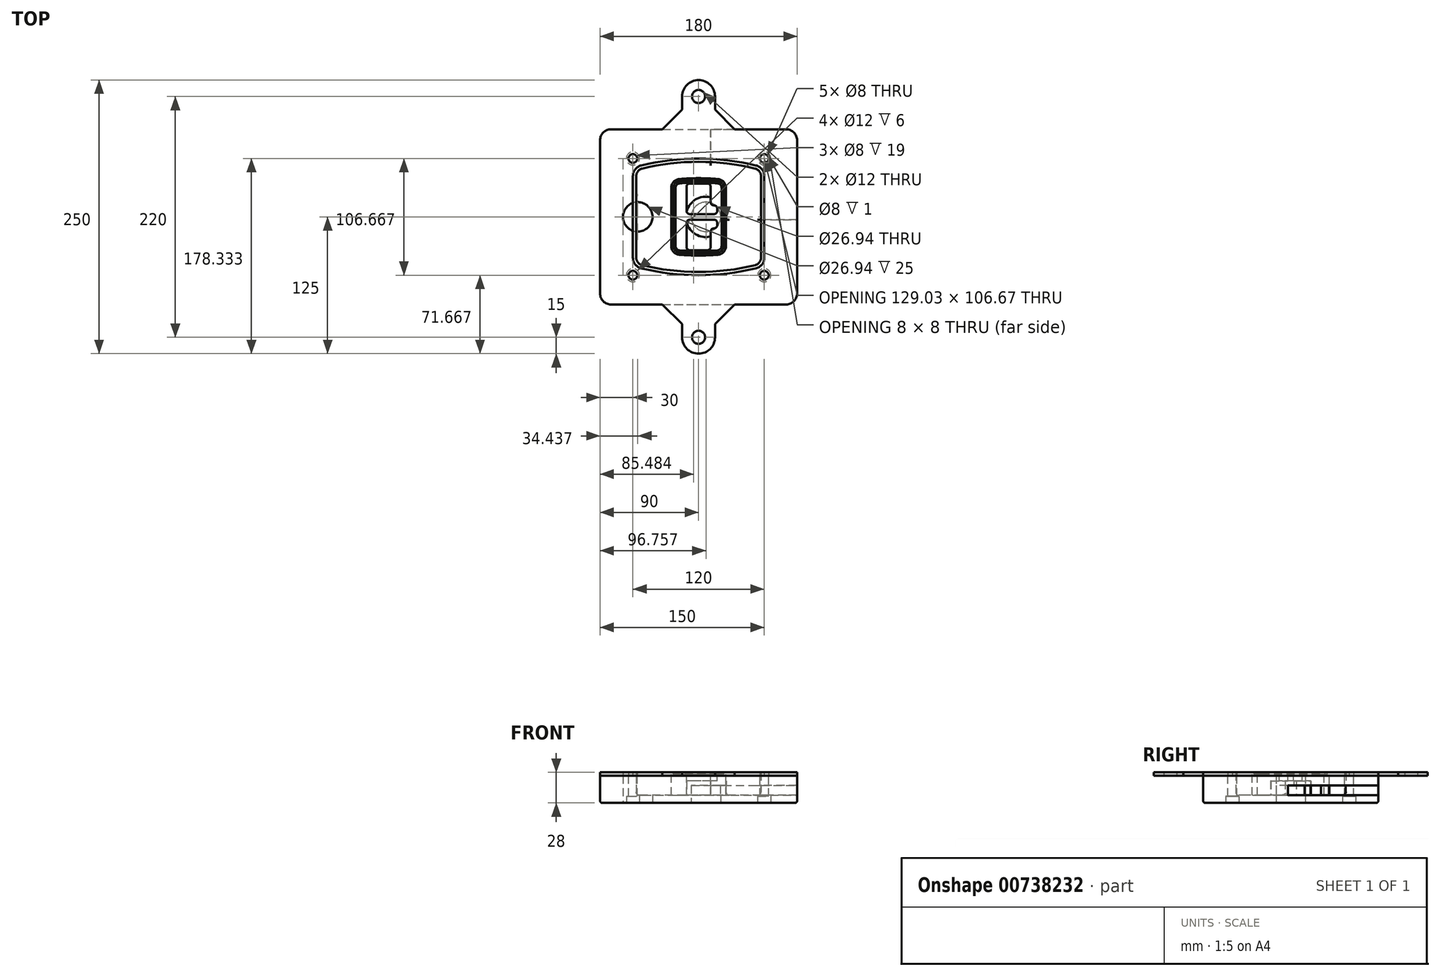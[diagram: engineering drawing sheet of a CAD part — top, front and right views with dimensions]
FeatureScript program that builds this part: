
annotation { "Feature Type Name" : "Feature", "Feature Type Description" : "" }
export const myFeature = defineFeature(function(context is Context, id is Id, definition is map)
    precondition{}
    {
        {
            var Q0;
            Q0=qCreatedBy(makeId("Top.planeOp"),FACE);
            var sketch = newSketch(context, id + "F0", { "sketchPlane" : qUnion([Q0])});
            skPoint(sketch, "E0.rect.middle", {"position": v(0, 0) * mm});
            skLineSegment(sketch, "E1.bottom", {"start": v(-80, -80) * mm, "end": v(80, -80) * mm});
            skLineSegment(sketch, "E1.top", {"start": v(-80, 80) * mm, "end": v(80, 80) * mm});
            skLineSegment(sketch, "E1.left", {"start": v(-90, -70) * mm, "end": v(-90, 70) * mm});
            skLineSegment(sketch, "E1.right", {"start": v(90, -70) * mm, "end": v(90, 70) * mm});
            skLineSegment(sketch, "E2", {"start": v(-90, 80) * mm, "end": v(90, -80) * mm, "construction": true});
            skLineSegment(sketch, "E3", {"start": v(90, 80) * mm, "end": v(-90, -80) * mm, "construction": true});
            skCircle(sketch, "E4", {"center": v(-60, 53.33) * mm, "radius": 4 * mm});
            skCircle(sketch, "E5", {"center": v(60, 53.33) * mm, "radius": 4 * mm});
            skCircle(sketch, "E6", {"center": v(60, -53.33) * mm, "radius": 4 * mm});
            skCircle(sketch, "E7", {"center": v(-60, -53.33) * mm, "radius": 4 * mm});
            skLineSegment(sketch, "E8", {"start": v(-60, 53.33) * mm, "end": v(60, 53.33) * mm, "construction": true});
            skLineSegment(sketch, "E9", {"start": v(60, 53.33) * mm, "end": v(60, -53.33) * mm, "construction": true});
            skLineSegment(sketch, "E10", {"start": v(60, -53.33) * mm, "end": v(-60, -53.33) * mm, "construction": true});
            skLineSegment(sketch, "E11", {"start": v(-60, -53.33) * mm, "end": v(-60, 53.33) * mm, "construction": true});
            skLineSegment(sketch, "E12", {"start": v(-60, 37.3) * mm, "end": v(-60, -37.3) * mm});
            skLineSegment(sketch, "E13", {"start": v(60, 37.3) * mm, "end": v(60, -37.3) * mm});
            skArc(sketch, "E14", {"start": v(52.38, 47.01) * mm, "mid": v(0, 53.33) * mm, "end": v(-52.38, 47.01) * mm});
            skArc(sketch, "E15", {"start": v(-52.38, -47.01) * mm, "mid": v(0, -53.33) * mm, "end": v(52.38, -47.01) * mm});
            skLineSegment(sketch, "E16", {"start": v(-60, 0) * mm, "end": v(60, 0) * mm, "construction": true});
            skPoint(sketch, "E17.visualSharp", {"position": v(-60, -45) * mm});
            skArc(sketch, "E17.filletArc", {"start": v(-60, -37.3) * mm, "mid": v(-57.87, -43.47) * mm, "end": v(-52.38, -47.01) * mm});
            skPoint(sketch, "E18.visualSharp", {"position": v(-60, 45) * mm});
            skArc(sketch, "E18.filletArc", {"start": v(-52.38, 47.01) * mm, "mid": v(-57.87, 43.47) * mm, "end": v(-60, 37.3) * mm});
            skPoint(sketch, "E19.visualSharp", {"position": v(60, 45) * mm});
            skArc(sketch, "E19.filletArc", {"start": v(60, 37.3) * mm, "mid": v(57.87, 43.47) * mm, "end": v(52.38, 47.01) * mm});
            skPoint(sketch, "E20.visualSharp", {"position": v(60, -45) * mm});
            skArc(sketch, "E20.filletArc", {"start": v(52.38, -47.01) * mm, "mid": v(57.87, -43.47) * mm, "end": v(60, -37.3) * mm});
            skPoint(sketch, "E21.visualSharp", {"position": v(-90, 80) * mm});
            skArc(sketch, "E21.filletArc", {"start": v(-80, 80) * mm, "mid": v(-87.07, 77.07) * mm, "end": v(-90, 70) * mm});
            skPoint(sketch, "E22.visualSharp", {"position": v(90, 80) * mm});
            skArc(sketch, "E22.filletArc", {"start": v(90, 70) * mm, "mid": v(87.07, 77.07) * mm, "end": v(80, 80) * mm});
            skPoint(sketch, "E23.visualSharp", {"position": v(90, -80) * mm});
            skArc(sketch, "E23.filletArc", {"start": v(80, -80) * mm, "mid": v(87.07, -77.07) * mm, "end": v(90, -70) * mm});
            skPoint(sketch, "E24.visualSharp", {"position": v(-90, -80) * mm});
            skArc(sketch, "E24.filletArc", {"start": v(-90, -70) * mm, "mid": v(-87.07, -77.07) * mm, "end": v(-80, -80) * mm});
            skArc(sketch, "E25.0", {"start": v(57, 37.3) * mm, "mid": v(55.5, 41.62) * mm, "end": v(51.67, 44.1) * mm});
            skLineSegment(sketch, "E25.1", {"start": v(57, 37.3) * mm, "end": v(57, -37.3) * mm});
            skArc(sketch, "E25.2", {"start": v(51.67, -44.1) * mm, "mid": v(55.5, -41.62) * mm, "end": v(57, -37.3) * mm});
            skArc(sketch, "E25.3", {"start": v(-51.67, -44.1) * mm, "mid": v(0, -50.33) * mm, "end": v(51.67, -44.1) * mm});
            skArc(sketch, "E25.4", {"start": v(-57, -37.3) * mm, "mid": v(-55.5, -41.62) * mm, "end": v(-51.67, -44.1) * mm});
            skArc(sketch, "E25.5", {"start": v(51.67, 44.1) * mm, "mid": v(0, 50.33) * mm, "end": v(-51.67, 44.1) * mm});
            skLineSegment(sketch, "E25.6", {"start": v(-57, 37.3) * mm, "end": v(-57, -37.3) * mm});
            skArc(sketch, "E25.7", {"start": v(-51.67, 44.1) * mm, "mid": v(-55.5, 41.62) * mm, "end": v(-57, 37.3) * mm});
            skArc(sketch, "E26.0", {"start": v(-53.33, 50.9) * mm, "mid": v(-61.01, 45.94) * mm, "end": v(-64, 37.3) * mm});
            skArc(sketch, "E26.1", {"start": v(53.33, 50.9) * mm, "mid": v(0, 57.33) * mm, "end": v(-53.33, 50.9) * mm});
            skArc(sketch, "E26.2", {"start": v(64, 37.3) * mm, "mid": v(61.01, 45.94) * mm, "end": v(53.33, 50.9) * mm});
            skLineSegment(sketch, "E26.3", {"start": v(64, 37.3) * mm, "end": v(64, -37.3) * mm});
            skArc(sketch, "E26.4", {"start": v(53.33, -50.9) * mm, "mid": v(61.01, -45.94) * mm, "end": v(64, -37.3) * mm});
            skLineSegment(sketch, "E26.5", {"start": v(-64, 37.3) * mm, "end": v(-64, -37.3) * mm});
            skArc(sketch, "E26.6", {"start": v(-53.33, -50.9) * mm, "mid": v(0, -57.33) * mm, "end": v(53.33, -50.9) * mm});
            skArc(sketch, "E26.7", {"start": v(-64, -37.3) * mm, "mid": v(-61.01, -45.94) * mm, "end": v(-53.33, -50.9) * mm});
            skSolve(sketch);
        }
        {
            var Q0;
            Q0=makeQuery(id+"F0.imprint","IMPRINT",FACE,{"disambiguationData":[TD([[makeQuery(id+"F0.imprint","IMPRINT",EDGE,{"derivedFrom":sQuery(id+"F0.wireOp",EDGE,"E1.bottom")}),1.0]])]});
            var Q1;
            Q1=makeQuery(id+"F0.imprint","IMPRINT",FACE,{"disambiguationData":[TD([[makeQuery(id+"F0.imprint","IMPRINT",EDGE,{"derivedFrom":sQuery(id+"F0.wireOp",EDGE,"E12")}),1.0]])]});
            var Q2;
            Q2=makeQuery(id+"F0.imprint","IMPRINT",FACE,{"disambiguationData":[TD([[makeQuery(id+"F0.imprint","IMPRINT",EDGE,{"derivedFrom":sQuery(id+"F0.wireOp",EDGE,"E25.0")}),1.0]])]});
            var Q3;
            Q3=makeQuery(id+"F0.imprint","IMPRINT",FACE,{"disambiguationData":[TD([[makeQuery(id+"F0.imprint","IMPRINT",EDGE,{"derivedFrom":sQuery(id+"F0.wireOp",EDGE,"E12")}),-1.0]])]});
            extrude(context, id + "F1", {"entities" : qUnion([Q0, Q1, Q2, Q3]), "oppositeDirection" : true, "depth" : 25 * mm});
        }
        {
            var Q0;
            Q0=makeQuery(id+"F0.imprint","IMPRINT",FACE,{"disambiguationData":[TD([[makeQuery(id+"F0.imprint","IMPRINT",EDGE,{"derivedFrom":sQuery(id+"F0.wireOp",EDGE,"E12")}),1.0]])]});
            extrude(context, id + "F2", {"entities" : qUnion([Q0]), "operationType" : NewBodyOperationType.ADD, "depth" : 3 * mm});
        }
        {
            var Q0;
            Q0=makeQuery(id+"F0.imprint","IMPRINT",FACE,{"disambiguationData":[TD([[makeQuery(id+"F0.imprint","IMPRINT",EDGE,{"derivedFrom":sQuery(id+"F0.wireOp",EDGE,"E25.0")}),1.0]])]});
            extrude(context, id + "F3", {"entities" : qUnion([Q0]), "operationType" : NewBodyOperationType.REMOVE, "oppositeDirection" : true, "depth" : 18 * mm});
        }
        {
            var Q0;
            Q0=makeQuery(id+"F2.opExtrude","CAP_FACE",FACE,{"disambiguationData":[OSD([sQuery(id+"F0.wireOp",EDGE,"E12"),sQuery(id+"F0.wireOp",EDGE,"E13"),sQuery(id+"F0.wireOp",EDGE,"E14"),sQuery(id+"F0.wireOp",EDGE,"E15"),sQuery(id+"F0.wireOp",EDGE,"E17.filletArc"),sQuery(id+"F0.wireOp",EDGE,"E18.filletArc"),sQuery(id+"F0.wireOp",EDGE,"E19.filletArc"),sQuery(id+"F0.wireOp",EDGE,"E20.filletArc"),sQuery(id+"F0.wireOp",EDGE,"E25.0"),sQuery(id+"F0.wireOp",EDGE,"E25.1"),sQuery(id+"F0.wireOp",EDGE,"E25.2"),sQuery(id+"F0.wireOp",EDGE,"E25.3"),sQuery(id+"F0.wireOp",EDGE,"E25.4"),sQuery(id+"F0.wireOp",EDGE,"E25.5"),sQuery(id+"F0.wireOp",EDGE,"E25.6"),sQuery(id+"F0.wireOp",EDGE,"E25.7")])],"isStart":false});
            var sketch = newSketch(context, id + "F4", { "sketchPlane" : qUnion([Q0])});
            skArc(sketch, "E27.0", {"start": v(-17.7, -34.56) * mm, "mid": v(0, -35.33) * mm, "end": v(17.7, -34.56) * mm});
            skArc(sketch, "E28.0", {"start": v(17.7, 34.56) * mm, "mid": v(0, 35.33) * mm, "end": v(-17.7, 34.56) * mm});
            skLineSegment(sketch, "E29", {"start": v(-25, 26.59) * mm, "end": v(-25, -26.59) * mm});
            skLineSegment(sketch, "E30", {"start": v(25, 26.59) * mm, "end": v(25, -26.59) * mm});
            skLineSegment(sketch, "E31", {"start": v(-25, 33.78) * mm, "end": v(25, 33.78) * mm, "construction": true});
            skLineSegment(sketch, "E32", {"start": v(-25, -33.78) * mm, "end": v(25, -33.78) * mm, "construction": true});
            skPoint(sketch, "E33.visualSharp", {"position": v(-25, 33.78) * mm});
            skArc(sketch, "E33.filletArc", {"start": v(-17.7, 34.56) * mm, "mid": v(-22.9, 32) * mm, "end": v(-25, 26.59) * mm});
            skPoint(sketch, "E34.visualSharp", {"position": v(25, 33.78) * mm});
            skArc(sketch, "E34.filletArc", {"start": v(25, 26.59) * mm, "mid": v(22.9, 32) * mm, "end": v(17.7, 34.56) * mm});
            skPoint(sketch, "E35.visualSharp", {"position": v(25, -33.78) * mm});
            skArc(sketch, "E35.filletArc", {"start": v(17.7, -34.56) * mm, "mid": v(22.9, -32) * mm, "end": v(25, -26.59) * mm});
            skPoint(sketch, "E36.visualSharp", {"position": v(-25, -33.78) * mm});
            skArc(sketch, "E36.filletArc", {"start": v(-25, -26.59) * mm, "mid": v(-22.9, -32) * mm, "end": v(-17.7, -34.56) * mm});
            skArc(sketch, "E37.0", {"start": v(51.67, 44.1) * mm, "mid": v(0, 50.33) * mm, "end": v(-51.67, 44.1) * mm});
            skArc(sketch, "E37.1", {"start": v(-51.67, 44.1) * mm, "mid": v(-55.5, 41.62) * mm, "end": v(-57, 37.3) * mm});
            skLineSegment(sketch, "E37.2", {"start": v(-57, 37.3) * mm, "end": v(-57, -37.3) * mm});
            skArc(sketch, "E37.3", {"start": v(-57, -37.3) * mm, "mid": v(-55.5, -41.62) * mm, "end": v(-51.67, -44.1) * mm});
            skArc(sketch, "E37.4", {"start": v(-51.67, -44.1) * mm, "mid": v(0, -50.33) * mm, "end": v(51.67, -44.1) * mm});
            skArc(sketch, "E37.5", {"start": v(51.67, -44.1) * mm, "mid": v(55.5, -41.62) * mm, "end": v(57, -37.3) * mm});
            skLineSegment(sketch, "E37.6", {"start": v(57, 37.3) * mm, "end": v(57, -37.3) * mm});
            skArc(sketch, "E37.7", {"start": v(57, 37.3) * mm, "mid": v(55.5, 41.62) * mm, "end": v(51.67, 44.1) * mm});
            skLineSegment(sketch, "E38.0", {"start": v(23, 26.59) * mm, "end": v(23, -26.59) * mm});
            skArc(sketch, "E38.1", {"start": v(17.53, -32.56) * mm, "mid": v(21.42, -30.64) * mm, "end": v(23, -26.59) * mm});
            skArc(sketch, "E38.2", {"start": v(-17.53, -32.56) * mm, "mid": v(0, -33.33) * mm, "end": v(17.53, -32.56) * mm});
            skArc(sketch, "E38.3", {"start": v(-23, -26.59) * mm, "mid": v(-21.42, -30.64) * mm, "end": v(-17.53, -32.56) * mm});
            skLineSegment(sketch, "E38.4", {"start": v(-23, 26.59) * mm, "end": v(-23, -26.59) * mm});
            skArc(sketch, "E38.5", {"start": v(23, 26.59) * mm, "mid": v(21.42, 30.64) * mm, "end": v(17.53, 32.56) * mm});
            skArc(sketch, "E38.6", {"start": v(-17.53, 32.56) * mm, "mid": v(-21.42, 30.64) * mm, "end": v(-23, 26.59) * mm});
            skArc(sketch, "E38.7", {"start": v(17.53, 32.56) * mm, "mid": v(0, 33.33) * mm, "end": v(-17.53, 32.56) * mm});
            skArc(sketch, "E39.0", {"start": v(21, 26.59) * mm, "mid": v(19.95, 29.29) * mm, "end": v(17.35, 30.57) * mm});
            skLineSegment(sketch, "E39.1", {"start": v(21, 26.59) * mm, "end": v(21, -26.59) * mm});
            skArc(sketch, "E39.2", {"start": v(17.35, -30.57) * mm, "mid": v(19.95, -29.29) * mm, "end": v(21, -26.59) * mm});
            skArc(sketch, "E39.3", {"start": v(-17.35, -30.57) * mm, "mid": v(0, -31.33) * mm, "end": v(17.35, -30.57) * mm});
            skArc(sketch, "E39.4", {"start": v(-21, -26.59) * mm, "mid": v(-19.95, -29.29) * mm, "end": v(-17.35, -30.57) * mm});
            skArc(sketch, "E39.5", {"start": v(17.35, 30.57) * mm, "mid": v(0, 31.33) * mm, "end": v(-17.35, 30.57) * mm});
            skLineSegment(sketch, "E39.6", {"start": v(-21, 26.59) * mm, "end": v(-21, -26.59) * mm});
            skArc(sketch, "E39.7", {"start": v(-17.35, 30.57) * mm, "mid": v(-19.95, 29.29) * mm, "end": v(-21, 26.59) * mm});
            skLineSegment(sketch, "E40", {"start": v(-25, 0) * mm, "end": v(25, 0) * mm, "construction": true});
            skLineSegment(sketch, "E41", {"start": v(-11, 5.5) * mm, "end": v(-11, 27.5) * mm});
            skLineSegment(sketch, "E42", {"start": v(-8, 30.5) * mm, "end": v(8, 30.5) * mm});
            skLineSegment(sketch, "E43", {"start": v(11, 27.5) * mm, "end": v(11, 13.5) * mm});
            skLineSegment(sketch, "E44", {"start": v(14, 10.5) * mm, "end": v(14, 10.5) * mm});
            skLineSegment(sketch, "E45", {"start": v(17, 7.5) * mm, "end": v(17, 5.5) * mm});
            skLineSegment(sketch, "E46", {"start": v(14, 2.5) * mm, "end": v(-8, 2.5) * mm});
            skPoint(sketch, "E47.visualSharp", {"position": v(-11, 30.5) * mm});
            skArc(sketch, "E47.filletArc", {"start": v(-8, 30.5) * mm, "mid": v(-10.12, 29.62) * mm, "end": v(-11, 27.5) * mm});
            skPoint(sketch, "E48.visualSharp", {"position": v(11, 30.5) * mm});
            skArc(sketch, "E48.filletArc", {"start": v(11, 27.5) * mm, "mid": v(10.12, 29.62) * mm, "end": v(8, 30.5) * mm});
            skPoint(sketch, "E49.visualSharp", {"position": v(11, 10.5) * mm});
            skArc(sketch, "E49.filletArc", {"start": v(11, 13.5) * mm, "mid": v(11.88, 11.38) * mm, "end": v(14, 10.5) * mm});
            skPoint(sketch, "E50.visualSharp", {"position": v(17, 10.5) * mm});
            skArc(sketch, "E50.filletArc", {"start": v(17, 7.5) * mm, "mid": v(16.12, 9.62) * mm, "end": v(14, 10.5) * mm});
            skPoint(sketch, "E51.visualSharp", {"position": v(17, 2.5) * mm});
            skArc(sketch, "E51.filletArc", {"start": v(14, 2.5) * mm, "mid": v(16.12, 3.38) * mm, "end": v(17, 5.5) * mm});
            skPoint(sketch, "E52.visualSharp", {"position": v(-11, 2.5) * mm});
            skArc(sketch, "E52.filletArc", {"start": v(-11, 5.5) * mm, "mid": v(-10.12, 3.38) * mm, "end": v(-8, 2.5) * mm});
            skLineSegment(sketch, "E53.0.MirrorCS", {"start": v(14, -2.5) * mm, "end": v(-8, -2.5) * mm});
            skArc(sketch, "E54.0.MirrorCS", {"start": v(-11, -5.5) * mm, "mid": v(-10.12, -3.38) * mm, "end": v(-8, -2.5) * mm});
            skLineSegment(sketch, "E55.0.MirrorCS", {"start": v(-11, -5.5) * mm, "end": v(-11, -27.5) * mm});
            skArc(sketch, "E56.0.MirrorCS", {"start": v(-8, -30.5) * mm, "mid": v(-10.12, -29.62) * mm, "end": v(-11, -27.5) * mm});
            skLineSegment(sketch, "E57.0.MirrorCS", {"start": v(-8, -30.5) * mm, "end": v(8, -30.5) * mm});
            skArc(sketch, "E58.0.MirrorCS", {"start": v(11, -27.5) * mm, "mid": v(10.12, -29.62) * mm, "end": v(8, -30.5) * mm});
            skLineSegment(sketch, "E59.0.MirrorCS", {"start": v(11, -27.5) * mm, "end": v(11, -13.5) * mm});
            skArc(sketch, "E60.0.MirrorCS", {"start": v(11, -13.5) * mm, "mid": v(11.88, -11.38) * mm, "end": v(14, -10.5) * mm});
            skArc(sketch, "E61.0.MirrorCS", {"start": v(17, -7.5) * mm, "mid": v(16.12, -9.62) * mm, "end": v(14, -10.5) * mm});
            skLineSegment(sketch, "E62.0.MirrorCS", {"start": v(17, -7.5) * mm, "end": v(17, -5.5) * mm});
            skArc(sketch, "E63.0.MirrorCS", {"start": v(14, -2.5) * mm, "mid": v(16.12, -3.38) * mm, "end": v(17, -5.5) * mm});
            skSolve(sketch);
        }
        {
            var Q0;
            Q0=makeQuery(id+"F4.imprint","IMPRINT",FACE,{"disambiguationData":[TD([[makeQuery(id+"F4.imprint","IMPRINT",EDGE,{"derivedFrom":sQuery(id+"F4.wireOp",EDGE,"E27.0")}),1.0]])]});
            var Q1;
            Q1=makeQuery(id+"F4.imprint","IMPRINT",FACE,{"disambiguationData":[TD([[makeQuery(id+"F4.imprint","IMPRINT",EDGE,{"derivedFrom":sQuery(id+"F4.wireOp",EDGE,"E38.0")}),-1.0]])]});
            var Q2;
            Q2=makeQuery(id+"F4.imprint","IMPRINT",FACE,{"disambiguationData":[TD([[makeQuery(id+"F4.imprint","IMPRINT",EDGE,{"derivedFrom":sQuery(id+"F4.wireOp",EDGE,"E39.0")}),1.0]])]});
            extrude(context, id + "F5", {"entities" : qUnion([Q0, Q1, Q2]), "operationType" : NewBodyOperationType.ADD, "endBound" : BoundingType.UP_TO_NEXT, "oppositeDirection" : true, "depth" : 25 * mm});
        }
        {
            var Q0;
            Q0=makeQuery(id+"F4.imprint","IMPRINT",FACE,{"disambiguationData":[TD([[makeQuery(id+"F4.imprint","IMPRINT",EDGE,{"derivedFrom":sQuery(id+"F4.wireOp",EDGE,"E38.0")}),-1.0]])]});
            extrude(context, id + "F6", {"entities" : qUnion([Q0]), "operationType" : NewBodyOperationType.REMOVE, "oppositeDirection" : true, "depth" : 2 * mm});
        }
        {
            var Q0;
            Q0=makeQuery(id+"F1.opExtrude","CAP_FACE",FACE,{"disambiguationData":[OSD([sQuery(id+"F0.wireOp",EDGE,"E1.bottom"),sQuery(id+"F0.wireOp",EDGE,"E1.top"),sQuery(id+"F0.wireOp",EDGE,"E1.left"),sQuery(id+"F0.wireOp",EDGE,"E1.right"),sQuery(id+"F0.wireOp",EDGE,"E4"),sQuery(id+"F0.wireOp",EDGE,"E5"),sQuery(id+"F0.wireOp",EDGE,"E6"),sQuery(id+"F0.wireOp",EDGE,"E7"),sQuery(id+"F0.wireOp",EDGE,"E21.filletArc"),sQuery(id+"F0.wireOp",EDGE,"E22.filletArc"),sQuery(id+"F0.wireOp",EDGE,"E23.filletArc"),sQuery(id+"F0.wireOp",EDGE,"E24.filletArc")])],"isStart":false});
            var sketch = newSketch(context, id + "F7", { "sketchPlane" : qUnion([Q0])});
            skCircle(sketch, "E64", {"center": v(6.76, 0) * mm, "radius": 13.47 * mm});
            skCircle(sketch, "E65", {"center": v(-55.56, 0) * mm, "radius": 13.47 * mm});
            skLineSegment(sketch, "E66", {"start": v(90, 0) * mm, "end": v(-90, 0) * mm});
            skCircle(sketch, "E67", {"center": v(6.76, 0) * mm, "radius": 18.47 * mm});
            skCircle(sketch, "E68", {"center": v(60, -53.33) * mm, "radius": 6 * mm});
            skCircle(sketch, "E69", {"center": v(-60, -53.33) * mm, "radius": 6 * mm});
            skCircle(sketch, "E70", {"center": v(-60, 53.33) * mm, "radius": 6 * mm});
            skCircle(sketch, "E71", {"center": v(60, 53.33) * mm, "radius": 6 * mm});
            skSolve(sketch);
        }
        {
            var Q0;
            {var subQ1=sQuery(id+"F7.wireOp",EDGE,"E66");var subQ4=sQuery(id+"F7.wireOp",EDGE,"E64");var subQ6=makeQuery(id+"F7.imprint","INTERSECT",VERTEX,{"disambiguationData":[OD(0.0)],"derivedFrom":[subQ4,subQ1]});Q0=makeQuery(id+"F7.imprint","IMPRINT",FACE,{"disambiguationData":[TD([[makeQuery(id+"F7.imprint","IMPRINT",EDGE,{"disambiguationData":[TD([[subQ6,-1.0]])],"derivedFrom":subQ4}),-1.0]])]});}
            var Q1;
            {var subQ0=sQuery(id+"F7.wireOp",EDGE,"E66");var subQ1=sQuery(id+"F7.wireOp",EDGE,"E64");var subQ3=makeQuery(id+"F7.imprint","INTERSECT",VERTEX,{"disambiguationData":[OD(0.0)],"derivedFrom":[subQ1,subQ0]});Q1=makeQuery(id+"F7.imprint","IMPRINT",FACE,{"disambiguationData":[TD([[makeQuery(id+"F7.imprint","IMPRINT",EDGE,{"disambiguationData":[TD([[subQ3,-1.0]])],"derivedFrom":subQ1}),1.0]])]});}
            var Q2;
            {var subQ0=sQuery(id+"F7.wireOp",EDGE,"E66");var subQ1=sQuery(id+"F7.wireOp",EDGE,"E64");var subQ3=makeQuery(id+"F7.imprint","INTERSECT",VERTEX,{"disambiguationData":[OD(0.0)],"derivedFrom":[subQ1,subQ0]});Q2=makeQuery(id+"F7.imprint","IMPRINT",FACE,{"disambiguationData":[TD([[makeQuery(id+"F7.imprint","IMPRINT",EDGE,{"disambiguationData":[TD([[subQ3,1.0]])],"derivedFrom":subQ1}),1.0]])]});}
            var Q3;
            {var subQ1=sQuery(id+"F7.wireOp",EDGE,"E66");var subQ4=sQuery(id+"F7.wireOp",EDGE,"E64");var subQ6=makeQuery(id+"F7.imprint","INTERSECT",VERTEX,{"disambiguationData":[OD(0.0)],"derivedFrom":[subQ4,subQ1]});Q3=makeQuery(id+"F7.imprint","IMPRINT",FACE,{"disambiguationData":[TD([[makeQuery(id+"F7.imprint","IMPRINT",EDGE,{"disambiguationData":[TD([[subQ6,1.0]])],"derivedFrom":subQ4}),-1.0]])]});}
            extrude(context, id + "F8", {"entities" : qUnion([Q0, Q1, Q2, Q3]), "operationType" : NewBodyOperationType.ADD, "oppositeDirection" : true, "depth" : 20 * mm});
        }
        {
            var Q0;
            {var subQ0=sQuery(id+"F7.wireOp",EDGE,"E66");var subQ1=sQuery(id+"F7.wireOp",EDGE,"E64");var subQ3=makeQuery(id+"F7.imprint","INTERSECT",VERTEX,{"disambiguationData":[OD(0.0)],"derivedFrom":[subQ1,subQ0]});Q0=makeQuery(id+"F7.imprint","IMPRINT",FACE,{"disambiguationData":[TD([[makeQuery(id+"F7.imprint","IMPRINT",EDGE,{"disambiguationData":[TD([[subQ3,-1.0]])],"derivedFrom":subQ1}),1.0]])]});}
            var Q1;
            {var subQ0=sQuery(id+"F7.wireOp",EDGE,"E66");var subQ1=sQuery(id+"F7.wireOp",EDGE,"E64");var subQ3=makeQuery(id+"F7.imprint","INTERSECT",VERTEX,{"disambiguationData":[OD(0.0)],"derivedFrom":[subQ1,subQ0]});Q1=makeQuery(id+"F7.imprint","IMPRINT",FACE,{"disambiguationData":[TD([[makeQuery(id+"F7.imprint","IMPRINT",EDGE,{"disambiguationData":[TD([[subQ3,1.0]])],"derivedFrom":subQ1}),1.0]])]});}
            extrude(context, id + "F9", {"entities" : qUnion([Q0, Q1]), "operationType" : NewBodyOperationType.REMOVE, "oppositeDirection" : true, "depth" : 16 * mm});
        }
        {
            var Q0;
            {var subQ0=sQuery(id+"F7.wireOp",EDGE,"E66");var subQ1=sQuery(id+"F7.wireOp",EDGE,"E65");var subQ3=makeQuery(id+"F7.imprint","INTERSECT",VERTEX,{"disambiguationData":[OD(0.0)],"derivedFrom":[subQ1,subQ0]});Q0=makeQuery(id+"F7.imprint","IMPRINT",FACE,{"disambiguationData":[TD([[makeQuery(id+"F7.imprint","IMPRINT",EDGE,{"disambiguationData":[TD([[subQ3,-1.0]])],"derivedFrom":subQ1}),1.0]])]});}
            var Q1;
            {var subQ0=sQuery(id+"F7.wireOp",EDGE,"E66");var subQ1=sQuery(id+"F7.wireOp",EDGE,"E65");var subQ3=makeQuery(id+"F7.imprint","INTERSECT",VERTEX,{"disambiguationData":[OD(0.0)],"derivedFrom":[subQ1,subQ0]});Q1=makeQuery(id+"F7.imprint","IMPRINT",FACE,{"disambiguationData":[TD([[makeQuery(id+"F7.imprint","IMPRINT",EDGE,{"disambiguationData":[TD([[subQ3,1.0]])],"derivedFrom":subQ1}),1.0]])]});}
            extrude(context, id + "F10", {"entities" : qUnion([Q0, Q1]), "operationType" : NewBodyOperationType.REMOVE, "oppositeDirection" : true, "depth" : 25 * mm});
        }
        {
            var Q0;
            Q0=makeQuery(id+"F7.imprint","IMPRINT",FACE,{"disambiguationData":[TD([[makeQuery(id+"F7.imprint","IMPRINT",EDGE,{"derivedFrom":sQuery(id+"F7.wireOp",EDGE,"E68")}),1.0]])]});
            var Q1;
            Q1=makeQuery(id+"F7.imprint","IMPRINT",FACE,{"disambiguationData":[TD([[makeQuery(id+"F7.imprint","IMPRINT",EDGE,{"derivedFrom":makeQuery(id+"F1.opExtrude","CAP_EDGE",EDGE,{"disambiguationData":[OSD([sQuery(id+"F0.wireOp",EDGE,"E5")])],"isStart":false})}),-1.0]])]});
            var Q2;
            Q2=makeQuery(id+"F7.imprint","IMPRINT",FACE,{"disambiguationData":[TD([[makeQuery(id+"F7.imprint","IMPRINT",EDGE,{"derivedFrom":sQuery(id+"F7.wireOp",EDGE,"E69")}),1.0]])]});
            var Q3;
            Q3=makeQuery(id+"F7.imprint","IMPRINT",FACE,{"disambiguationData":[TD([[makeQuery(id+"F7.imprint","IMPRINT",EDGE,{"derivedFrom":makeQuery(id+"F1.opExtrude","CAP_EDGE",EDGE,{"disambiguationData":[OSD([sQuery(id+"F0.wireOp",EDGE,"E4")])],"isStart":false})}),-1.0]])]});
            var Q4;
            Q4=makeQuery(id+"F7.imprint","IMPRINT",FACE,{"disambiguationData":[TD([[makeQuery(id+"F7.imprint","IMPRINT",EDGE,{"derivedFrom":sQuery(id+"F7.wireOp",EDGE,"E70")}),1.0]])]});
            var Q5;
            Q5=makeQuery(id+"F7.imprint","IMPRINT",FACE,{"disambiguationData":[TD([[makeQuery(id+"F7.imprint","IMPRINT",EDGE,{"derivedFrom":makeQuery(id+"F1.opExtrude","CAP_EDGE",EDGE,{"disambiguationData":[OSD([sQuery(id+"F0.wireOp",EDGE,"E7")])],"isStart":false})}),-1.0]])]});
            var Q6;
            Q6=makeQuery(id+"F7.imprint","IMPRINT",FACE,{"disambiguationData":[TD([[makeQuery(id+"F7.imprint","IMPRINT",EDGE,{"derivedFrom":sQuery(id+"F7.wireOp",EDGE,"E71")}),1.0]])]});
            var Q7;
            Q7=makeQuery(id+"F7.imprint","IMPRINT",FACE,{"disambiguationData":[TD([[makeQuery(id+"F7.imprint","IMPRINT",EDGE,{"derivedFrom":makeQuery(id+"F1.opExtrude","CAP_EDGE",EDGE,{"disambiguationData":[OSD([sQuery(id+"F0.wireOp",EDGE,"E6")])],"isStart":false})}),-1.0]])]});
            extrude(context, id + "F11", {"entities" : qUnion([Q0, Q1, Q2, Q3, Q4, Q5, Q6, Q7]), "operationType" : NewBodyOperationType.REMOVE, "oppositeDirection" : true, "depth" : 6 * mm});
        }
        {
            var Q0;
            Q0=makeQuery(id+"F9.boolean.opBoolean","COPY",FACE,{"derivedFrom":makeQuery(id+"F9.opExtrude","CAP_FACE",FACE,{"disambiguationData":[OSD([sQuery(id+"F7.wireOp",EDGE,"E64")])],"isStart":false})});
            var sketch = newSketch(context, id + "F12", { "sketchPlane" : qUnion([Q0])});
            skArc(sketch, "E72.0", {"start": v(11, -88.19) * mm, "mid": v(97.1, -83.6) * mm, "end": v(92.5, 2.5) * mm});
            skLineSegment(sketch, "E72.1", {"start": v(11, -17.97) * mm, "end": v(11, -17.97) * mm});
            skLineSegment(sketch, "E73", {"start": v(92.5, -105.13) * mm, "end": v(102.3, -105.13) * mm});
            skLineSegment(sketch, "E74.0", {"start": v(92.5, 2.5) * mm, "end": v(14, 2.5) * mm});
            skArc(sketch, "E74.1", {"start": v(14, 2.5) * mm, "mid": v(16.12, 3.38) * mm, "end": v(17, 5.5) * mm});
            skLineSegment(sketch, "E74.2", {"start": v(17, 7.5) * mm, "end": v(17, 5.5) * mm});
            skArc(sketch, "E74.3", {"start": v(17, 7.5) * mm, "mid": v(16.12, 9.62) * mm, "end": v(14, 10.5) * mm});
            skArc(sketch, "E74.4", {"start": v(11, 13.5) * mm, "mid": v(11.88, 11.38) * mm, "end": v(14, 10.5) * mm});
            skLineSegment(sketch, "E74.5", {"start": v(11, 13.5) * mm, "end": v(11, -88.19) * mm});
            skLineSegment(sketch, "E74.7", {"start": v(92.5, -2.5) * mm, "end": v(14, -2.5) * mm});
            skArc(sketch, "E74.8", {"start": v(14, -2.5) * mm, "mid": v(16.12, -3.38) * mm, "end": v(17, -5.5) * mm});
            skLineSegment(sketch, "E74.9", {"start": v(17, -7.5) * mm, "end": v(17, -5.5) * mm});
            skArc(sketch, "E74.10", {"start": v(17, -7.5) * mm, "mid": v(16.12, -9.62) * mm, "end": v(14, -10.5) * mm});
            skArc(sketch, "E74.11", {"start": v(11, -13.5) * mm, "mid": v(11.88, -11.38) * mm, "end": v(14, -10.5) * mm});
            skLineSegment(sketch, "E74.12", {"start": v(11, -17.97) * mm, "end": v(11, -13.5) * mm});
            skPoint(sketch, "E75.orphan", {"position": v(11, -27.5) * mm});
            skPoint(sketch, "E76.orphan", {"position": v(-8, -2.5) * mm});
            skPoint(sketch, "E77.orphan", {"position": v(-8, 2.5) * mm});
            skPoint(sketch, "E78.orphan", {"position": v(11, 27.5) * mm});
            skSolve(sketch);
        }
        {
            var Q0;
            {var subQ7=sQuery(id+"F12.wireOp",EDGE,"E72.0");var subQ14=sQuery(id+"F12.wireOp",EDGE,"E72.1");var subQ16=sQuery(id+"F12.wireOp",EDGE,"E74.1");var subQ18=sQuery(id+"F12.wireOp",EDGE,"E74.8");Q0=qUnion([makeQuery(id+"F12.imprint","IMPRINT",FACE,{"disambiguationData":[TD([[makeQuery(id+"F12.imprint","IMPRINT",EDGE,{"derivedFrom":subQ7}),1.0]])]}),makeQuery(id+"F12.imprint","IMPRINT",FACE,{"disambiguationData":[TD([[makeQuery(id+"F12.imprint","IMPRINT",EDGE,{"derivedFrom":subQ14}),1.0]])]}),makeQuery(id+"F12.imprint","IMPRINT",FACE,{"disambiguationData":[TD([[makeQuery(id+"F12.imprint","IMPRINT",EDGE,{"derivedFrom":subQ16}),1.0]])]}),makeQuery(id+"F12.imprint","IMPRINT",FACE,{"disambiguationData":[TD([[makeQuery(id+"F12.imprint","IMPRINT",EDGE,{"derivedFrom":subQ18}),-1.0]])]})]);}
            var Q1;
            Q1=makeQuery(id+"F5.boolean.opBoolean","SPLIT",FACE,{"disambiguationData":[TD([makeQuery(id+"F5.opExtrude","SWEPT_FACE",FACE,{"disambiguationData":[OSD([sQuery(id+"F4.wireOp",EDGE,"E41")])]})])],"derivedFrom":makeQuery(id+"F3.boolean.opBoolean","COPY",FACE,{"derivedFrom":makeQuery(id+"F3.opExtrude","CAP_FACE",FACE,{"disambiguationData":[OSD([sQuery(id+"F0.wireOp",EDGE,"E25.0"),sQuery(id+"F0.wireOp",EDGE,"E25.1"),sQuery(id+"F0.wireOp",EDGE,"E25.2"),sQuery(id+"F0.wireOp",EDGE,"E25.3"),sQuery(id+"F0.wireOp",EDGE,"E25.4"),sQuery(id+"F0.wireOp",EDGE,"E25.5"),sQuery(id+"F0.wireOp",EDGE,"E25.6"),sQuery(id+"F0.wireOp",EDGE,"E25.7")])],"isStart":false})})});
            extrude(context, id + "F13", {"entities" : qUnion([Q0]), "operationType" : NewBodyOperationType.REMOVE, "endBound" : BoundingType.UP_TO_SURFACE, "endBoundEntityFace" : qUnion([Q1]), "depth" : 25 * mm});
        }
        {
            var Q0;
            Q0=makeQuery(id+"F3.boolean.opBoolean","COPY",EDGE,{"derivedFrom":makeQuery(id+"F3.opExtrude","CAP_EDGE",EDGE,{"disambiguationData":[OSD([sQuery(id+"F0.wireOp",EDGE,"E25.6")])],"isStart":false})});
            var Q1;
            Q1=makeQuery(id+"F8.boolean.opBoolean","INTERSECT",EDGE,{"derivedFrom":[makeQuery(id+"F5.opExtrude","SWEPT_FACE",FACE,{"disambiguationData":[OSD([sQuery(id+"F4.wireOp",EDGE,"E30")])]}),makeQuery(id+"F8.opExtrude","CAP_FACE",FACE,{"disambiguationData":[OSD([sQuery(id+"F7.wireOp",EDGE,"E67")])],"isStart":false})]});
            var Q2;
            Q2=makeQuery(id+"F8.boolean.opBoolean","INTERSECT",EDGE,{"disambiguationData":[OD(1.0)],"derivedFrom":[makeQuery(id+"F5.opExtrude","SWEPT_FACE",FACE,{"disambiguationData":[OSD([sQuery(id+"F4.wireOp",EDGE,"E30")])]}),makeQuery(id+"F8.opExtrude","SWEPT_FACE",FACE,{"disambiguationData":[OSD([sQuery(id+"F7.wireOp",EDGE,"E67")])]})]});
            var Q3;
            {var subQ0=makeQuery(id+"F3.boolean.opBoolean","COPY",FACE,{"derivedFrom":makeQuery(id+"F3.opExtrude","CAP_FACE",FACE,{"disambiguationData":[OSD([sQuery(id+"F0.wireOp",EDGE,"E25.0"),sQuery(id+"F0.wireOp",EDGE,"E25.1"),sQuery(id+"F0.wireOp",EDGE,"E25.2"),sQuery(id+"F0.wireOp",EDGE,"E25.3"),sQuery(id+"F0.wireOp",EDGE,"E25.4"),sQuery(id+"F0.wireOp",EDGE,"E25.5"),sQuery(id+"F0.wireOp",EDGE,"E25.6"),sQuery(id+"F0.wireOp",EDGE,"E25.7")])],"isStart":false})});var subQ1=sQuery(id+"F4.wireOp",EDGE,"E30");Q3=makeQuery(id+"F8.boolean.opBoolean","SPLIT",EDGE,{"disambiguationData":[TD([makeQuery(id+"F5.opExtrude","SWEPT_FACE",FACE,{"disambiguationData":[OSD([sQuery(id+"F4.wireOp",EDGE,"E35.filletArc")])]})])],"derivedFrom":makeQuery(id+"F5.opExtrude","TWEAK_EDGE",EDGE,{"derivedFrom":[subQ0,makeQuery(id+"F4.imprint","IMPRINT",EDGE,{"derivedFrom":subQ1})]})});}
            var Q4;
            {var subQ0=sQuery(id+"F0.wireOp",EDGE,"E25.0");var subQ1=sQuery(id+"F0.wireOp",EDGE,"E25.1");var subQ2=sQuery(id+"F0.wireOp",EDGE,"E25.2");var subQ3=sQuery(id+"F0.wireOp",EDGE,"E25.3");var subQ4=sQuery(id+"F0.wireOp",EDGE,"E25.4");var subQ5=sQuery(id+"F0.wireOp",EDGE,"E25.5");var subQ6=sQuery(id+"F0.wireOp",EDGE,"E25.6");var subQ7=sQuery(id+"F0.wireOp",EDGE,"E25.7");Q4=makeQuery(id+"F8.boolean.opBoolean","INTERSECT",EDGE,{"derivedFrom":[makeQuery(id+"F5.boolean.opBoolean","SPLIT",FACE,{"disambiguationData":[TD([makeQuery(id+"F2.opExtrude","SWEPT_FACE",FACE,{"disambiguationData":[OSD([subQ0])]})])],"derivedFrom":makeQuery(id+"F3.boolean.opBoolean","COPY",FACE,{"derivedFrom":makeQuery(id+"F3.opExtrude","CAP_FACE",FACE,{"disambiguationData":[OSD([subQ0,subQ1,subQ2,subQ3,subQ4,subQ5,subQ6,subQ7])],"isStart":false})})}),makeQuery(id+"F8.opExtrude","SWEPT_FACE",FACE,{"disambiguationData":[OSD([sQuery(id+"F7.wireOp",EDGE,"E67")])]})]});}
            var Q5;
            Q5=makeQuery(id+"F8.boolean.opBoolean","INTERSECT",EDGE,{"disambiguationData":[OD(0.0)],"derivedFrom":[makeQuery(id+"F5.opExtrude","SWEPT_FACE",FACE,{"disambiguationData":[OSD([sQuery(id+"F4.wireOp",EDGE,"E30")])]}),makeQuery(id+"F8.opExtrude","SWEPT_FACE",FACE,{"disambiguationData":[OSD([sQuery(id+"F7.wireOp",EDGE,"E67")])]})]});
            fillet(context, id + "F14", {"entities" : qUnion([Q0, Q1, Q2, Q3, Q4, Q5]), "radius" : 3 * mm, "tangentPropagation" : true, "allowEdgeOverflow" : false});
        }
        {
            var Q0;
            Q0=makeQuery(id+"F1.opExtrude","CAP_EDGE",EDGE,{"disambiguationData":[OSD([sQuery(id+"F0.wireOp",EDGE,"E1.bottom")])],"isStart":false});
            fillet(context, id + "F15", {"entities" : qUnion([Q0]), "radius" : 2 * mm, "tangentPropagation" : true, "allowEdgeOverflow" : false});
        }
        {
            var Q0;
            {var subQ0=sQuery(id+"F0.wireOp",EDGE,"E21.filletArc");var subQ1=sQuery(id+"F0.wireOp",EDGE,"E7");var subQ2=sQuery(id+"F0.wireOp",EDGE,"E6");var subQ3=sQuery(id+"F0.wireOp",EDGE,"E5");var subQ4=sQuery(id+"F0.wireOp",EDGE,"E4");var subQ5=sQuery(id+"F0.wireOp",EDGE,"E22.filletArc");var subQ6=sQuery(id+"F0.wireOp",EDGE,"E1.bottom");var subQ7=sQuery(id+"F0.wireOp",EDGE,"E1.right");var subQ8=sQuery(id+"F0.wireOp",EDGE,"E1.top");var subQ9=sQuery(id+"F0.wireOp",EDGE,"E1.left");var subQ10=sQuery(id+"F0.wireOp",EDGE,"E23.filletArc");var subQ11=sQuery(id+"F0.wireOp",EDGE,"E24.filletArc");Q0=makeQuery(id+"F2.boolean.opBoolean","SPLIT",FACE,{"disambiguationData":[TD([makeQuery(id+"F1.opExtrude","SWEPT_FACE",FACE,{"disambiguationData":[OSD([subQ6])]})])],"derivedFrom":makeQuery(id+"F1.opExtrude","CAP_FACE",FACE,{"disambiguationData":[OSD([subQ6,subQ8,subQ9,subQ7,subQ4,subQ3,subQ2,subQ1,subQ0,subQ5,subQ10,subQ11])],"isStart":true})});}
            var sketch = newSketch(context, id + "F16", { "sketchPlane" : qUnion([Q0])});
            skLineSegment(sketch, "E79.0", {"start": v(-80, 80) * mm, "end": v(80, 80) * mm});
            skLineSegment(sketch, "E79.1", {"start": v(-90, -70) * mm, "end": v(-90, 70) * mm});
            skArc(sketch, "E79.2", {"start": v(-80, 80) * mm, "mid": v(-87.07, 77.07) * mm, "end": v(-90, 70) * mm});
            skArc(sketch, "E79.3", {"start": v(-90, -70) * mm, "mid": v(-87.07, -77.07) * mm, "end": v(-80, -80) * mm});
            skLineSegment(sketch, "E79.4", {"start": v(-80, -80) * mm, "end": v(80, -80) * mm});
            skArc(sketch, "E79.5", {"start": v(80, -80) * mm, "mid": v(87.07, -77.07) * mm, "end": v(90, -70) * mm});
            skLineSegment(sketch, "E79.6", {"start": v(90, -70) * mm, "end": v(90, 70) * mm});
            skArc(sketch, "E79.7", {"start": v(90, 70) * mm, "mid": v(87.07, 77.07) * mm, "end": v(80, 80) * mm});
            skCircle(sketch, "E79.9", {"center": v(-60, 53.33) * mm, "radius": 4 * mm});
            skCircle(sketch, "E79.10", {"center": v(-60, -53.33) * mm, "radius": 4 * mm});
            skCircle(sketch, "E79.11", {"center": v(60, 53.33) * mm, "radius": 4 * mm});
            skCircle(sketch, "E79.12", {"center": v(60, -53.33) * mm, "radius": 4 * mm});
            skLineSegment(sketch, "E80", {"start": v(0, 80) * mm, "end": v(0, 110) * mm, "construction": true});
            skLineSegment(sketch, "E81", {"start": v(-33, 80) * mm, "end": v(-15, 98) * mm});
            skLineSegment(sketch, "E82", {"start": v(-15, 98) * mm, "end": v(-15, 110) * mm});
            skArc(sketch, "E83", {"start": v(-15, 110) * mm, "mid": v(0, 125) * mm, "end": v(15, 110) * mm});
            skLineSegment(sketch, "E84", {"start": v(15, 110) * mm, "end": v(15, 98) * mm});
            skLineSegment(sketch, "E85", {"start": v(15, 98) * mm, "end": v(33, 80) * mm});
            skCircle(sketch, "E86", {"center": v(0, 110) * mm, "radius": 6 * mm});
            skLineSegment(sketch, "E87", {"start": v(-90, 0) * mm, "end": v(90, 0) * mm, "construction": true});
            skPoint(sketch, "E87.startSnap0", {"position": v(-43.18, 0) * mm});
            skLineSegment(sketch, "E88.MirrorCS", {"start": v(-33, -80) * mm, "end": v(-15, -98) * mm});
            skLineSegment(sketch, "E89.MirrorCS", {"start": v(-15, -98) * mm, "end": v(-15, -110) * mm});
            skArc(sketch, "E90.MirrorCS", {"start": v(-15, -110) * mm, "mid": v(0, -125) * mm, "end": v(15, -110) * mm});
            skCircle(sketch, "E91.MirrorC", {"center": v(0, -110) * mm, "radius": 6 * mm});
            skLineSegment(sketch, "E92.MirrorCS", {"start": v(0, -80) * mm, "end": v(0, -110) * mm, "construction": true});
            skLineSegment(sketch, "E93.MirrorCS", {"start": v(15, -98) * mm, "end": v(33, -80) * mm});
            skLineSegment(sketch, "E94.MirrorCS", {"start": v(15, -110) * mm, "end": v(15, -98) * mm});
            skSolve(sketch);
        }
        {
            var Q0;
            {var subQ0=sQuery(id+"F16.wireOp",EDGE,"E81");Q0=makeQuery(id+"F16.imprint","IMPRINT",FACE,{"disambiguationData":[TD([[makeQuery(id+"F16.imprint","IMPRINT",EDGE,{"derivedFrom":subQ0}),-1.0]])]});}
            var Q1;
            Q1=makeQuery(id+"F16.imprint","IMPRINT",FACE,{"disambiguationData":[TD([[makeQuery(id+"F16.imprint","IMPRINT",EDGE,{"derivedFrom":sQuery(id+"F16.wireOp",EDGE,"E79.1")}),-1.0]])]});
            var Q2;
            {var subQ0=sQuery(id+"F16.wireOp",EDGE,"E88.MirrorCS");Q2=makeQuery(id+"F16.imprint","IMPRINT",FACE,{"disambiguationData":[TD([[makeQuery(id+"F16.imprint","IMPRINT",EDGE,{"derivedFrom":subQ0}),1.0]])]});}
            var Q3;
            Q3=makeQuery(id+"F2.opExtrude","CAP_FACE",FACE,{"disambiguationData":[OSD([sQuery(id+"F0.wireOp",EDGE,"E12"),sQuery(id+"F0.wireOp",EDGE,"E13"),sQuery(id+"F0.wireOp",EDGE,"E14"),sQuery(id+"F0.wireOp",EDGE,"E15"),sQuery(id+"F0.wireOp",EDGE,"E17.filletArc"),sQuery(id+"F0.wireOp",EDGE,"E18.filletArc"),sQuery(id+"F0.wireOp",EDGE,"E19.filletArc"),sQuery(id+"F0.wireOp",EDGE,"E20.filletArc"),sQuery(id+"F0.wireOp",EDGE,"E25.0"),sQuery(id+"F0.wireOp",EDGE,"E25.1"),sQuery(id+"F0.wireOp",EDGE,"E25.2"),sQuery(id+"F0.wireOp",EDGE,"E25.3"),sQuery(id+"F0.wireOp",EDGE,"E25.4"),sQuery(id+"F0.wireOp",EDGE,"E25.5"),sQuery(id+"F0.wireOp",EDGE,"E25.6"),sQuery(id+"F0.wireOp",EDGE,"E25.7")])],"isStart":false});
            extrude(context, id + "F17", {"entities" : qUnion([Q0, Q1, Q2]), "endBound" : BoundingType.UP_TO_SURFACE, "depth" : 25 * mm, "endBoundEntityFace" : qUnion([Q3]), "offsetDistance" : 25 * mm});
        }
    });
